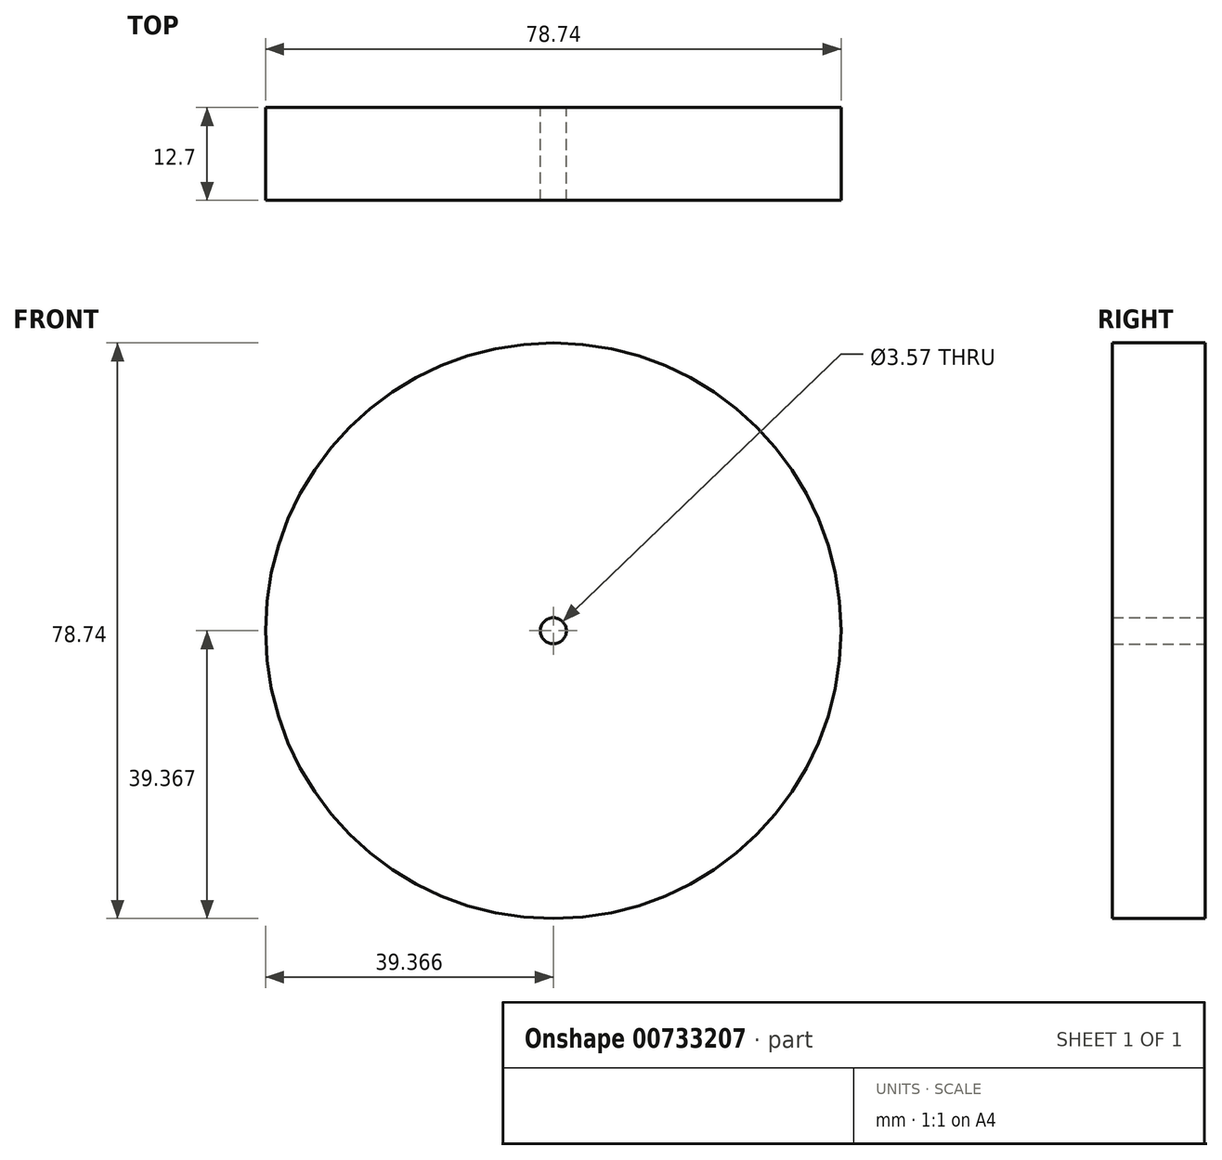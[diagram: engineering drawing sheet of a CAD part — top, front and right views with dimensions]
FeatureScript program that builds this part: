
annotation { "Feature Type Name" : "Feature", "Feature Type Description" : "" }
export const myFeature = defineFeature(function(context is Context, id is Id, definition is map)
    precondition{}
    {
        {
            var Q0;
            Q0=qCreatedBy(makeId("Front.planeOp"),FACE);
            var sketch = newSketch(context, id + "F0", { "sketchPlane" : qUnion([Q0])});
            skCircle(sketch, "E0", {"center": v(-39.55, 33.24) * mm, "radius": 39.37 * mm});
            skCircle(sketch, "E1", {"center": v(-39.55, 33.24) * mm, "radius": 1.79 * mm});
            skSolve(sketch);
        }
        {
            var Q0;
            Q0=makeQuery(id+"F0.imprint","IMPRINT",FACE,{"disambiguationData":[TD([[makeQuery(id+"F0.imprint","IMPRINT",EDGE,{"derivedFrom":sQuery(id+"F0.wireOp",EDGE,"E0")}),1.0]])]});
            extrude(context, id + "F1", {"entities" : qUnion([Q0]), "depth" : 12.7 * mm, "offsetDistance" : 25.4 * mm});
        }
    });
